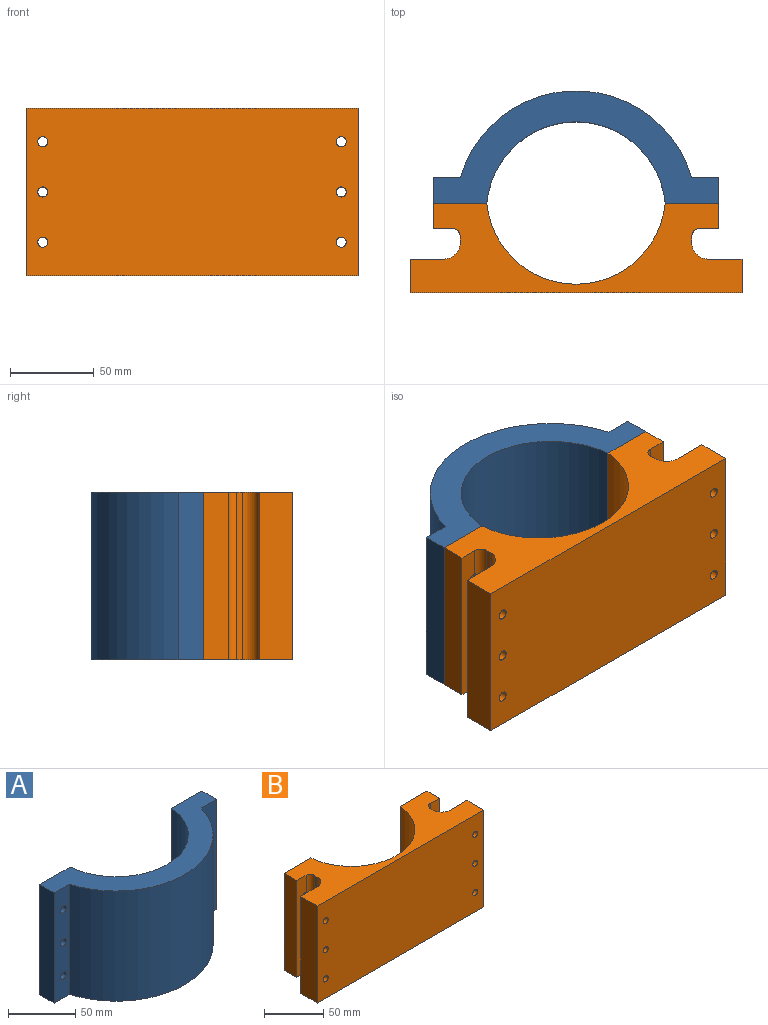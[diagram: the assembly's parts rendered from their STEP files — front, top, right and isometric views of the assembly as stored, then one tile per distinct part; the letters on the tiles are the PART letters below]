
ASSEMBLY  parts=2 mates=1
PART A: 16 faces, bbox 170x67x100 mm
  f0: cylinder r=53.5mm len=106.53mm, axis (0,0,-1), area 15806.1mm2, adj f1,f7,f8,f9
  f1: plane 100x31.73mm, normal (0,1,0), area 3088.6mm2, adj f0,f2,f8,f9,f10,f11,f12
  f2: plane 100x15mm, normal (-1,0,0), area 1500mm2, adj f1,f3,f8,f9
  f3: plane 100x15.87mm, normal (0,-1,0), area 1501.9mm2, adj f2,f4,f8,f9,f10,f11,f12
  f4: cylinder r=71.97mm len=138.27mm, axis (0,0,-1), area 18556mm2, adj f3,f5,f8,f9
  f5: plane 100x15.87mm, normal (0,-1,0), area 1501.9mm2, adj f4,f6,f8,f9,f13,f14,f15
  f6: plane 100x15mm, normal (1,0,0), area 1500mm2, adj f5,f7,f8,f9
  f7: plane 100x31.73mm, normal (0,1,0), area 3088.6mm2, adj f0,f6,f8,f9,f13,f14,f15
  f8: plane 170x66.97mm, normal (0,0,1), area 3882.7mm2, adj f0,f1,f2,f3,f4,f5,f6,f7
  f9: plane 170x66.97mm, normal (0,0,-1), area 3882.7mm2, adj f0,f1,f2,f3,f4,f5,f6,f7
  f10: cylinder r=3mm len=15mm, axis (0,1,0), area 282.7mm2, adj f1,f3
  f11: cylinder r=3mm len=15mm, axis (0,1,0), area 282.7mm2, adj f1,f3
  f12: cylinder r=3mm len=15mm, axis (0,1,0), area 282.7mm2, adj f1,f3
  f13: cylinder r=3mm len=15mm, axis (0,1,0), area 282.7mm2, adj f5,f7
  f14: cylinder r=3mm len=15mm, axis (0,1,0), area 282.7mm2, adj f5,f7
  f15: cylinder r=3mm len=15mm, axis (0,1,0), area 282.7mm2, adj f5,f7
PART B: 38 faces, bbox 198.3x53.5x100 mm
  f0: plane 100x3.5mm, normal (1,0,0), area 350mm2, adj f14,f15,f16,f37
  f1: plane 100x10.87mm, normal (0,-1,0), area 1028.9mm2, adj f2,f14,f15,f16,f25,f27,f29
  f2: plane 100x15mm, normal (1,0,0), area 1500mm2, adj f1,f3,f14,f15
  f3: plane 100x31.73mm, normal (0,1,0), area 3088.6mm2, adj f2,f4,f14,f15,f25,f27,f29
  f4: cylinder r=53.5mm len=106.53mm, axis (0,0,-1), area 15806.1mm2, adj f3,f5,f14,f15
  f5: plane 100x31.73mm, normal (0,1,0), area 3088.6mm2, adj f4,f6,f14,f15,f19,f21,f23
  f6: plane 100x15mm, normal (-1,0,0), area 1500mm2, adj f5,f7,f14,f15
  f7: plane 100x10.87mm, normal (0,-1,0), area 1028.9mm2, adj f6,f14,f15,f17,f19,f21,f23
  f8: plane 100x3.5mm, normal (-1,0,0), area 350mm2, adj f14,f15,f17,f36
  f9: plane 100x20mm, normal (0,1,0), area 1915.2mm2, adj f10,f14,f15,f33,f34,f35,f36
  f10: plane 100x20mm, normal (-1,0,0), area 2000mm2, adj f9,f11,f14,f15
  f11: plane 198.27x100mm, normal (0,-1,0), area 19656.9mm2, adj f10,f12,f14,f15,f30,f31,f32,f33
  f12: plane 100x20mm, normal (1,0,0), area 2000mm2, adj f11,f13,f14,f15
  f13: plane 100x20mm, normal (0,1,0), area 1915.2mm2, adj f12,f14,f15,f30,f31,f32,f37
  f14: plane 198.27x53.5mm, normal (0,0,1), area 5165.1mm2, adj f0,f1,f2,f3,f4,f5,f6,f7
  f15: plane 198.27x53.5mm, normal (0,0,-1), area 5165.1mm2, adj f0,f1,f2,f3,f4,f5,f6,f7
  f16: cylinder r=5mm len=100mm, axis (0,0,-1), area 785.4mm2, adj f0,f1,f14,f15,f24,f26,f28
  f17: cylinder r=5mm len=100mm, axis (0,0,1), area 785.4mm2, adj f7,f8,f14,f15,f18,f20,f22
  f18: plane 5.74x2.13mm, normal (0,1,0), area 9mm2, adj f17,f19
  f19: cylinder r=3mm len=15mm, axis (0,1,0), area 282.7mm2, adj f5,f7,f18
  f20: plane 5.74x2.13mm, normal (0,1,0), area 9mm2, adj f17,f21
  f21: cylinder r=3mm len=15mm, axis (0,1,0), area 282.7mm2, adj f5,f7,f20
  f22: plane 5.74x2.13mm, normal (0,1,0), area 9mm2, adj f17,f23
  f23: cylinder r=3mm len=15mm, axis (0,1,0), area 282.7mm2, adj f5,f7,f22
  f24: plane 5.74x2.13mm, normal (0,1,0), area 9mm2, adj f16,f25
  f25: cylinder r=3mm len=15mm, axis (0,1,0), area 282.7mm2, adj f1,f3,f24
  f26: plane 5.74x2.13mm, normal (0,1,0), area 9mm2, adj f16,f27
  f27: cylinder r=3mm len=15mm, axis (0,1,0), area 282.7mm2, adj f1,f3,f26
  f28: plane 5.74x2.13mm, normal (0,1,0), area 9mm2, adj f16,f29
  f29: cylinder r=3mm len=15mm, axis (0,1,0), area 282.7mm2, adj f1,f3,f28
  f30: cylinder r=3mm len=20mm, axis (0,-1,0), area 377mm2, adj f11,f13
  f31: cylinder r=3mm len=20mm, axis (0,-1,0), area 377mm2, adj f11,f13
  f32: cylinder r=3mm len=20mm, axis (0,-1,0), area 377mm2, adj f11,f13
  f33: cylinder r=3mm len=20mm, axis (0,-1,0), area 377mm2, adj f9,f11
  f34: cylinder r=3mm len=20mm, axis (0,-1,0), area 377mm2, adj f9,f11
  f35: cylinder r=3mm len=20mm, axis (0,-1,0), area 377mm2, adj f9,f11
  f36: cylinder r=10mm len=100mm, axis (0,0,-1), area 1570.8mm2, adj f8,f9,f14,f15
  f37: cylinder r=10mm len=100mm, axis (0,0,1), area 1570.8mm2, adj f0,f13,f14,f15
PLACE A rot(axis=(1,0,0),180deg) t=(-60.6,3.81,63.07)mm
PLACE B t=(-60.6,13.81,-36.93)mm
MATE slider A.f11 <-> B.f23  axis (0,-1,0) through (-135.6,8.81,43.07)mm
